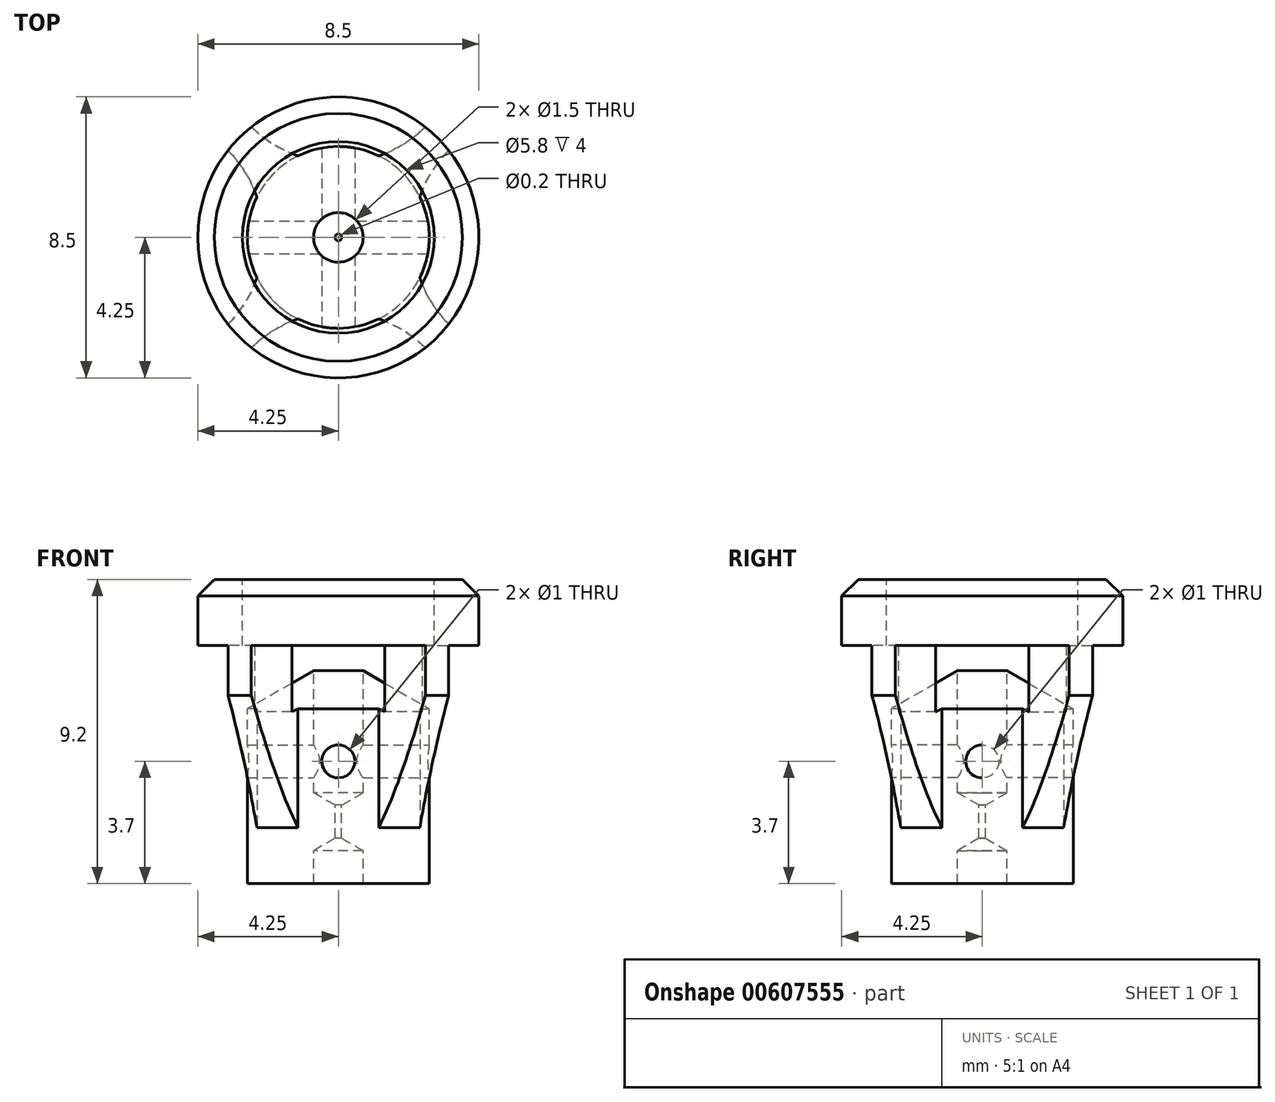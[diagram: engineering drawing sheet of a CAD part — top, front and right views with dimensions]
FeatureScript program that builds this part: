
annotation { "Feature Type Name" : "Feature", "Feature Type Description" : "" }
export const myFeature = defineFeature(function(context is Context, id is Id, definition is map)
    precondition{}
    {
        {
            var Q0;
            Q0=qCreatedBy(makeId("Front.planeOp"),FACE);
            var sketch = newSketch(context, id + "F0", { "sketchPlane" : qUnion([Q0])});
            skLineSegment(sketch, "E0", {"start": v(0, 0) * mm, "end": v(2.75, 0) * mm});
            skLineSegment(sketch, "E1", {"start": v(2.75, 0) * mm, "end": v(2.75, 0) * mm});
            skLineSegment(sketch, "E2", {"start": v(2.75, 0) * mm, "end": v(2.75, 1.7) * mm});
            skLineSegment(sketch, "E3", {"start": v(2.75, 1.7) * mm, "end": v(4.25, 5.7) * mm});
            skLineSegment(sketch, "E4", {"start": v(4.25, 5.7) * mm, "end": v(4.25, 9.2) * mm});
            skLineSegment(sketch, "E5", {"start": v(4.25, 9.2) * mm, "end": v(0, 9.2) * mm});
            skLineSegment(sketch, "E6", {"start": v(0, 9.2) * mm, "end": v(0, 0) * mm});
            skLineSegment(sketch, "E7", {"start": v(0.75, 0) * mm, "end": v(0.75, 1) * mm});
            skLineSegment(sketch, "E8", {"start": v(0.75, 1) * mm, "end": v(0.75, 1) * mm});
            skLineSegment(sketch, "E9", {"start": v(0.75, 1) * mm, "end": v(0.1, 1.38) * mm});
            skLineSegment(sketch, "E10", {"start": v(0.1, 1.38) * mm, "end": v(0.1, 2.38) * mm});
            skLineSegment(sketch, "E11", {"start": v(0.1, 2.38) * mm, "end": v(0.75, 2.75) * mm});
            skLineSegment(sketch, "E12", {"start": v(0.75, 2.75) * mm, "end": v(0.75, 6.44) * mm});
            skLineSegment(sketch, "E13", {"start": v(0.75, 6.44) * mm, "end": v(2.9, 5.2) * mm});
            skLineSegment(sketch, "E14", {"start": v(2.9, 5.2) * mm, "end": v(2.9, 5.2) * mm});
            skLineSegment(sketch, "E15", {"start": v(2.9, 5.2) * mm, "end": v(2.9, 9.2) * mm});
            skSolve(sketch);
        }
        {
            var Q0;
            {var subQ4=sQuery(id+"F0.wireOp",EDGE,"E2");Q0=makeQuery(id+"F0.imprint","IMPRINT",FACE,{"disambiguationData":[TD([[makeQuery(id+"F0.imprint","IMPRINT",EDGE,{"derivedFrom":subQ4}),1.0]])]});}
            var Q1;
            Q1=sQuery(id+"F0.wireOp",EDGE,"E6");
            revolve(context, id + "F1", {"entities" : qUnion([Q0]), "axis" : qUnion([Q1]), "revolveType" : RevolveType.FULL});
        }
        {
            var Q0;
            Q0=qCreatedBy(makeId("Front.planeOp"),FACE);
            var sketch = newSketch(context, id + "F2", { "sketchPlane" : qUnion([Q0])});
            skCircle(sketch, "E16", {"center": v(0, 3.7) * mm, "radius": 0.5 * mm});
            skSolve(sketch);
        }
        {
            var Q0;
            Q0 = qSketchRegion(id + "F2", true);
            extrude(context, id + "F3", {"entities" : qUnion([Q0]), "operationType" : NewBodyOperationType.REMOVE, "endBound" : BoundingType.THROUGH_ALL, "oppositeDirection" : true, "depth" : 25 * mm, "offsetDistance" : 25 * mm, "hasSecondDirection" : true, "secondDirectionBound" : SecondDirectionBoundingType.THROUGH_ALL, "secondDirectionOppositeDirection" : false, "secondDirectionDepth" : 25 * mm});
        }
        {
            var Q0;
            Q0=qCreatedBy(makeId("Right.planeOp"),FACE);
            var sketch = newSketch(context, id + "F4", { "sketchPlane" : qUnion([Q0])});
            skCircle(sketch, "E17", {"center": v(0, 3.7) * mm, "radius": 0.5 * mm});
            skSolve(sketch);
        }
        {
            var Q0;
            Q0 = qSketchRegion(id + "F4", true);
            extrude(context, id + "F5", {"entities" : qUnion([Q0]), "operationType" : NewBodyOperationType.REMOVE, "endBound" : BoundingType.THROUGH_ALL, "oppositeDirection" : true, "depth" : 25 * mm, "offsetDistance" : 25 * mm, "hasSecondDirection" : true, "secondDirectionBound" : SecondDirectionBoundingType.THROUGH_ALL, "secondDirectionOppositeDirection" : false, "secondDirectionDepth" : 25 * mm});
        }
        {
            var Q0;
            Q0=qCreatedBy(makeId("Top.planeOp"),FACE);
            var sketch = newSketch(context, id + "F6", { "sketchPlane" : qUnion([Q0])});
            skCircle(sketch, "E18", {"center": v(0, 0) * mm, "radius": 6.01 * mm});
            skCircle(sketch, "E19", {"center": v(0, -6.01) * mm, "radius": 3.75 * mm});
            skCircle(sketch, "E20", {"center": v(-6.01, 0) * mm, "radius": 3.75 * mm});
            skCircle(sketch, "E21", {"center": v(6.01, 0) * mm, "radius": 3.75 * mm});
            skCircle(sketch, "E22", {"center": v(0, 6.01) * mm, "radius": 3.75 * mm});
            skLineSegment(sketch, "E23", {"start": v(0, 6.01) * mm, "end": v(6.01, 0) * mm});
            skCircle(sketch, "E24", {"center": v(0, 0) * mm, "radius": 2.75 * mm});
            skSolve(sketch);
        }
        {
            var Q0;
            {var subQ0=sQuery(id+"F6.wireOp",EDGE,"E23");var subQ1=sQuery(id+"F6.wireOp",EDGE,"E18");var subQ2=makeQuery(id+"F6.imprint","INTERSECT",VERTEX,{"disambiguationData":[OD(1.0)],"derivedFrom":[subQ1,subQ0]});Q0=makeQuery(id+"F6.imprint","IMPRINT",FACE,{"disambiguationData":[TD([[makeQuery(id+"F6.imprint","IMPRINT",EDGE,{"disambiguationData":[TD([[subQ2,1.0]])],"derivedFrom":subQ1}),1.0]])]});}
            var Q1;
            {var subQ0=sQuery(id+"F6.wireOp",EDGE,"E23");var subQ1=sQuery(id+"F6.wireOp",EDGE,"E18");var subQ2=makeQuery(id+"F6.imprint","INTERSECT",VERTEX,{"disambiguationData":[OD(1.0)],"derivedFrom":[subQ1,subQ0]});Q1=makeQuery(id+"F6.imprint","IMPRINT",FACE,{"disambiguationData":[TD([[makeQuery(id+"F6.imprint","IMPRINT",EDGE,{"disambiguationData":[TD([[subQ2,-1.0]])],"derivedFrom":subQ1}),1.0]])]});}
            var Q2;
            {var subQ0=sQuery(id+"F6.wireOp",EDGE,"E19");var subQ1=sQuery(id+"F6.wireOp",EDGE,"E18");var subQ2=makeQuery(id+"F6.imprint","INTERSECT",VERTEX,{"disambiguationData":[OD(0.0)],"derivedFrom":[subQ1,subQ0]});Q2=makeQuery(id+"F6.imprint","IMPRINT",FACE,{"disambiguationData":[TD([[makeQuery(id+"F6.imprint","IMPRINT",EDGE,{"disambiguationData":[TD([[subQ2,-1.0]])],"derivedFrom":subQ1}),1.0]])]});}
            var Q3;
            {var subQ0=sQuery(id+"F6.wireOp",EDGE,"E20");var subQ1=sQuery(id+"F6.wireOp",EDGE,"E18");var subQ2=makeQuery(id+"F6.imprint","INTERSECT",VERTEX,{"disambiguationData":[OD(0.0)],"derivedFrom":[subQ1,subQ0]});Q3=makeQuery(id+"F6.imprint","IMPRINT",FACE,{"disambiguationData":[TD([[makeQuery(id+"F6.imprint","IMPRINT",EDGE,{"disambiguationData":[TD([[subQ2,-1.0]])],"derivedFrom":subQ1}),1.0]])]});}
            var Q4;
            {var subQ3=sQuery(id+"F6.wireOp",EDGE,"E23");var subQ5=sQuery(id+"F6.wireOp",EDGE,"E18");var subQ6=makeQuery(id+"F6.imprint","INTERSECT",VERTEX,{"disambiguationData":[OD(0.0)],"derivedFrom":[subQ5,subQ3]});Q4=makeQuery(id+"F6.imprint","IMPRINT",FACE,{"disambiguationData":[TD([[makeQuery(id+"F6.imprint","IMPRINT",EDGE,{"disambiguationData":[TD([[subQ6,-1.0]])],"derivedFrom":subQ5}),1.0]])]});}
            var Q5;
            {var subQ0=sQuery(id+"F6.wireOp",EDGE,"E23");var subQ1=sQuery(id+"F6.wireOp",EDGE,"E18");var subQ2=makeQuery(id+"F6.imprint","INTERSECT",VERTEX,{"disambiguationData":[OD(0.0)],"derivedFrom":[subQ1,subQ0]});Q5=makeQuery(id+"F6.imprint","IMPRINT",FACE,{"disambiguationData":[TD([[makeQuery(id+"F6.imprint","IMPRINT",EDGE,{"disambiguationData":[TD([[subQ2,1.0]])],"derivedFrom":subQ1}),1.0]])]});}
            extrude(context, id + "F7", {"entities" : qUnion([Q0, Q1, Q2, Q3, Q4, Q5]), "operationType" : NewBodyOperationType.REMOVE, "depth" : 7.2 * mm, "offsetDistance" : 25 * mm});
        }
        {
            var Q0;
            Q0=makeQuery(id+"F1.opRevolve","SWEPT_EDGE",EDGE,{"disambiguationData":[OSD([sQuery(id+"F0.wireOp",EDGE,"E4"),sQuery(id+"F0.wireOp",EDGE,"E5")])]});
            chamfer(context, id + "F8", {"entities" : qUnion([Q0]), "chamferType" : ChamferType.OFFSET_ANGLE, "width" : 0.5 * mm, "oppositeDirection" : false, "angle" : 45 * degree, "tangentPropagation" : true});
        }
    });
